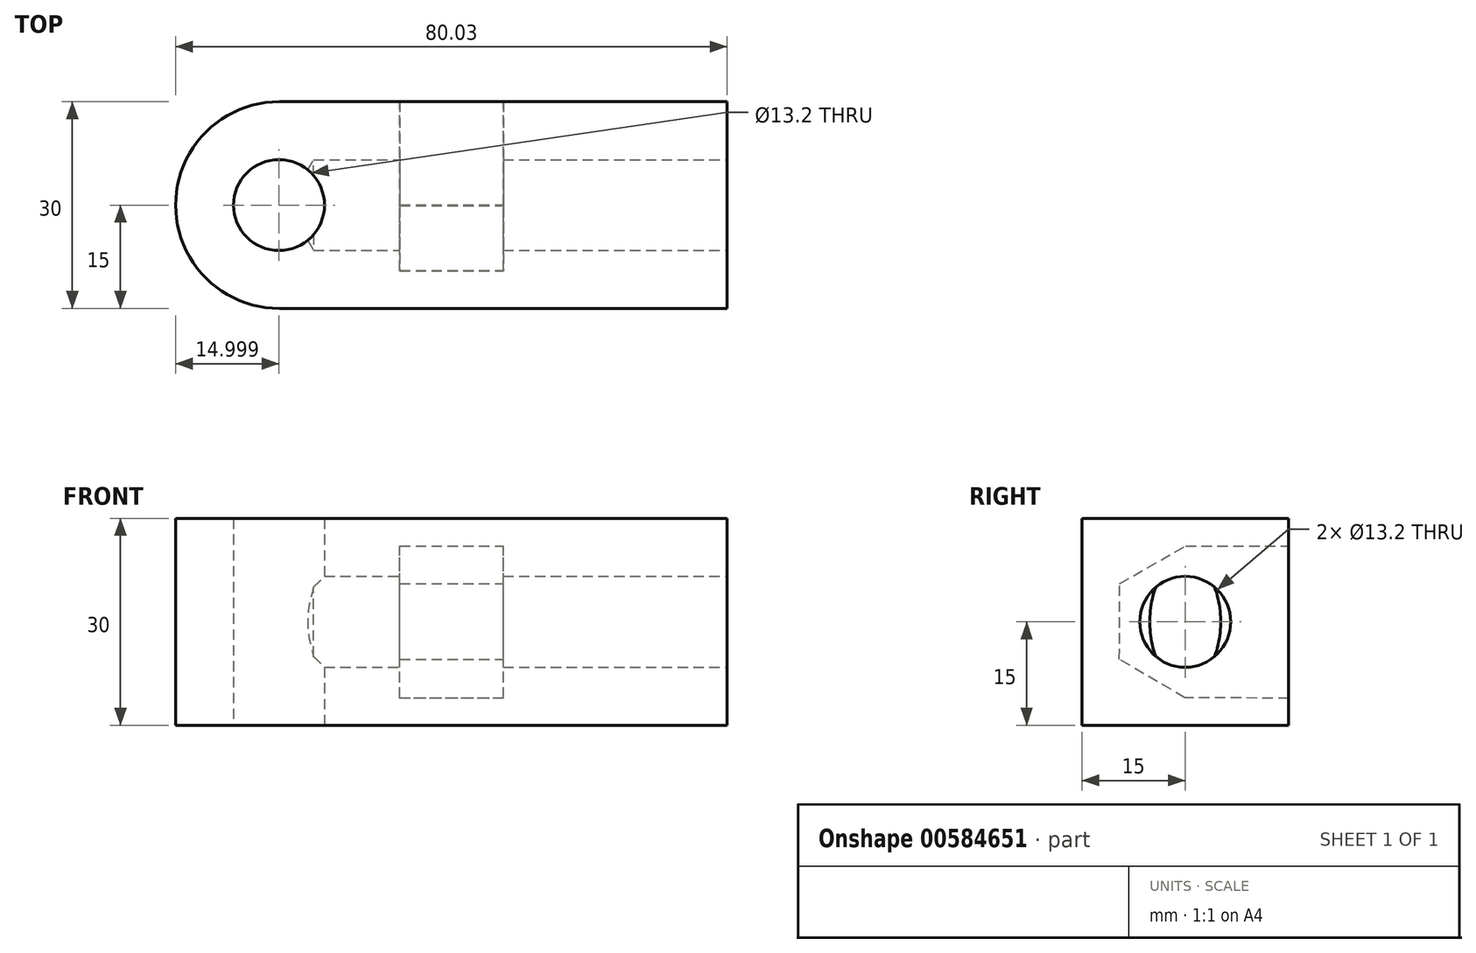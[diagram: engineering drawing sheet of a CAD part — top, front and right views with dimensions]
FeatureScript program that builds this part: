
annotation { "Feature Type Name" : "Feature", "Feature Type Description" : "" }
export const myFeature = defineFeature(function(context is Context, id is Id, definition is map)
    precondition{}
    {
        {
            var Q0;
            Q0=qCreatedBy(makeId("Top.planeOp"),FACE);
            var sketch = newSketch(context, id + "F0", { "sketchPlane" : qUnion([Q0])});
            skCircle(sketch, "E0", {"center": v(-32.53, 0) * mm, "radius": 15 * mm});
            skLineSegment(sketch, "E1.bottom", {"start": v(32.5, 15) * mm, "end": v(-32.5, 15) * mm});
            skLineSegment(sketch, "E1.top", {"start": v(32.5, -15) * mm, "end": v(-32.5, -15) * mm});
            skLineSegment(sketch, "E1.left", {"start": v(32.5, 15) * mm, "end": v(32.5, -15) * mm});
            skLineSegment(sketch, "E1.right", {"start": v(-32.5, 15) * mm, "end": v(-32.5, -15) * mm});
            skPoint(sketch, "E1.middle", {"position": v(0, 0) * mm});
            skSolve(sketch);
        }
        {
            var Q0;
            Q0=makeQuery(id+"F0.imprint","IMPRINT",FACE,{"disambiguationData":[TD([[makeQuery(id+"F0.imprint","IMPRINT",EDGE,{"derivedFrom":sQuery(id+"F0.wireOp",EDGE,"E0")}),1.0]])]});
            var Q1;
            {var subQ1=sQuery(id+"F0.wireOp",EDGE,"E1.bottom");Q1=makeQuery(id+"F0.imprint","IMPRINT",FACE,{"disambiguationData":[TD([[makeQuery(id+"F0.imprint","IMPRINT",EDGE,{"derivedFrom":subQ1}),1.0]])]});}
            extrude(context, id + "F1", {"entities" : qUnion([Q0, Q1]), "endBound" : BoundingType.SYMMETRIC, "depth" : 30 * mm, "offsetDistance" : 25 * mm});
        }
        {
            var Q0;
            Q0=qCreatedBy(makeId("Right.planeOp"),FACE);
            var sketch = newSketch(context, id + "F2", { "sketchPlane" : qUnion([Q0])});
            skCircle(sketch, "E2.cCircle", {"center": v(0, 0) * mm, "radius": 9.53 * mm, "construction": true});
            skLineSegment(sketch, "E2.0", {"start": v(9.5, -5.56) * mm, "end": v(-0.07, -11) * mm});
            skLineSegment(sketch, "E2.1", {"start": v(-0.07, -11) * mm, "end": v(-9.56, -5.44) * mm});
            skLineSegment(sketch, "E2.2", {"start": v(-9.56, -5.44) * mm, "end": v(-9.5, 5.56) * mm});
            skLineSegment(sketch, "E2.3", {"start": v(-9.5, 5.56) * mm, "end": v(0.07, 11) * mm});
            skLineSegment(sketch, "E2.4", {"start": v(0.07, 11) * mm, "end": v(9.56, 5.44) * mm});
            skLineSegment(sketch, "E2.5", {"start": v(9.56, 5.44) * mm, "end": v(9.5, -5.56) * mm});
            skPoint(sketch, "E2.0.midPoint", {"position": v(4.71, -8.28) * mm});
            skLineSegment(sketch, "E3", {"start": v(0.07, 11) * mm, "end": v(17.53, 11) * mm});
            skLineSegment(sketch, "E4", {"start": v(17.53, 11) * mm, "end": v(17.53, -11.12) * mm});
            skLineSegment(sketch, "E5", {"start": v(17.53, -11.12) * mm, "end": v(-0.07, -11) * mm});
            skSolve(sketch);
        }
        {
            var Q0;
            Q0 = qSketchRegion(id + "F2", true);
            extrude(context, id + "F3", {"entities" : qUnion([Q0]), "operationType" : NewBodyOperationType.REMOVE, "oppositeDirection" : true, "depth" : 15 * mm, "offsetDistance" : 25 * mm});
        }
        {
            var Q0;
            Q0=makeQuery(id+"F1.opExtrude","CAP_FACE",FACE,{"disambiguationData":[OSD([sQuery(id+"F0.wireOp",EDGE,"E0"),sQuery(id+"F0.wireOp",EDGE,"E1.bottom"),sQuery(id+"F0.wireOp",EDGE,"E1.top"),sQuery(id+"F0.wireOp",EDGE,"E1.left")])],"isStart":true});
            var sketch = newSketch(context, id + "F4", { "sketchPlane" : qUnion([Q0])});
            skPoint(sketch, "E6", {"position": v(-32.53, 0) * mm});
            skSolve(sketch);
        }
        {
            var Q0;
            Q0=sQuery(id+"F4.wireOp",VERTEX,"E6");
            var Q1;
            Q1=makeQuery(id+"F1.opExtrude","SWEPT_BODY",BODY,{"disambiguationData":[OSD([sQuery(id+"F0.wireOp",EDGE,"E0"),sQuery(id+"F0.wireOp",EDGE,"E1.bottom"),sQuery(id+"F0.wireOp",EDGE,"E1.top"),sQuery(id+"F0.wireOp",EDGE,"E1.left")])]});
            hole(context, id + "F5", {"style" : HoleStyle.C_BORE, "endStyle" : HoleEndStyle.BLIND, "holeDiameter" : 13.2 * mm, "cBoreDiameter" : 19.25 * mm, "cBoreDepth" : 0 * mm, "majorDiameter" : 5 * mm, "holeDepth" : 60 * mm, "isTappedThrough" : true, "tappedDepth" : 12 * mm, "tapClearance" : 3, "startFromSketch" : true, "locations" : qUnion([Q0]), "scope" : qUnion([Q1])});
        }
        {
            var Q0;
            Q0=makeQuery(id+"F1.opExtrude","SWEPT_FACE",FACE,{"disambiguationData":[OSD([sQuery(id+"F0.wireOp",EDGE,"E1.left")])]});
            var sketch = newSketch(context, id + "F6", { "sketchPlane" : qUnion([Q0])});
            skPoint(sketch, "E7", {"position": v(0, 0) * mm});
            skSolve(sketch);
        }
        {
            var Q0;
            Q0=sQuery(id+"F6.wireOp",VERTEX,"E7");
            var Q1;
            Q1=makeQuery(id+"F1.opExtrude","SWEPT_BODY",BODY,{"disambiguationData":[OSD([sQuery(id+"F0.wireOp",EDGE,"E0"),sQuery(id+"F0.wireOp",EDGE,"E1.bottom"),sQuery(id+"F0.wireOp",EDGE,"E1.top"),sQuery(id+"F0.wireOp",EDGE,"E1.left")])]});
            hole(context, id + "F7", {"style" : HoleStyle.C_BORE, "endStyle" : HoleEndStyle.BLIND, "holeDiameter" : 13.2 * mm, "cBoreDiameter" : 19.25 * mm, "cBoreDepth" : 0 * mm, "majorDiameter" : 5 * mm, "holeDepth" : 60 * mm, "isTappedThrough" : true, "tappedDepth" : 12 * mm, "tapClearance" : 3, "startFromSketch" : true, "locations" : qUnion([Q0]), "scope" : qUnion([Q1])});
        }
    });
